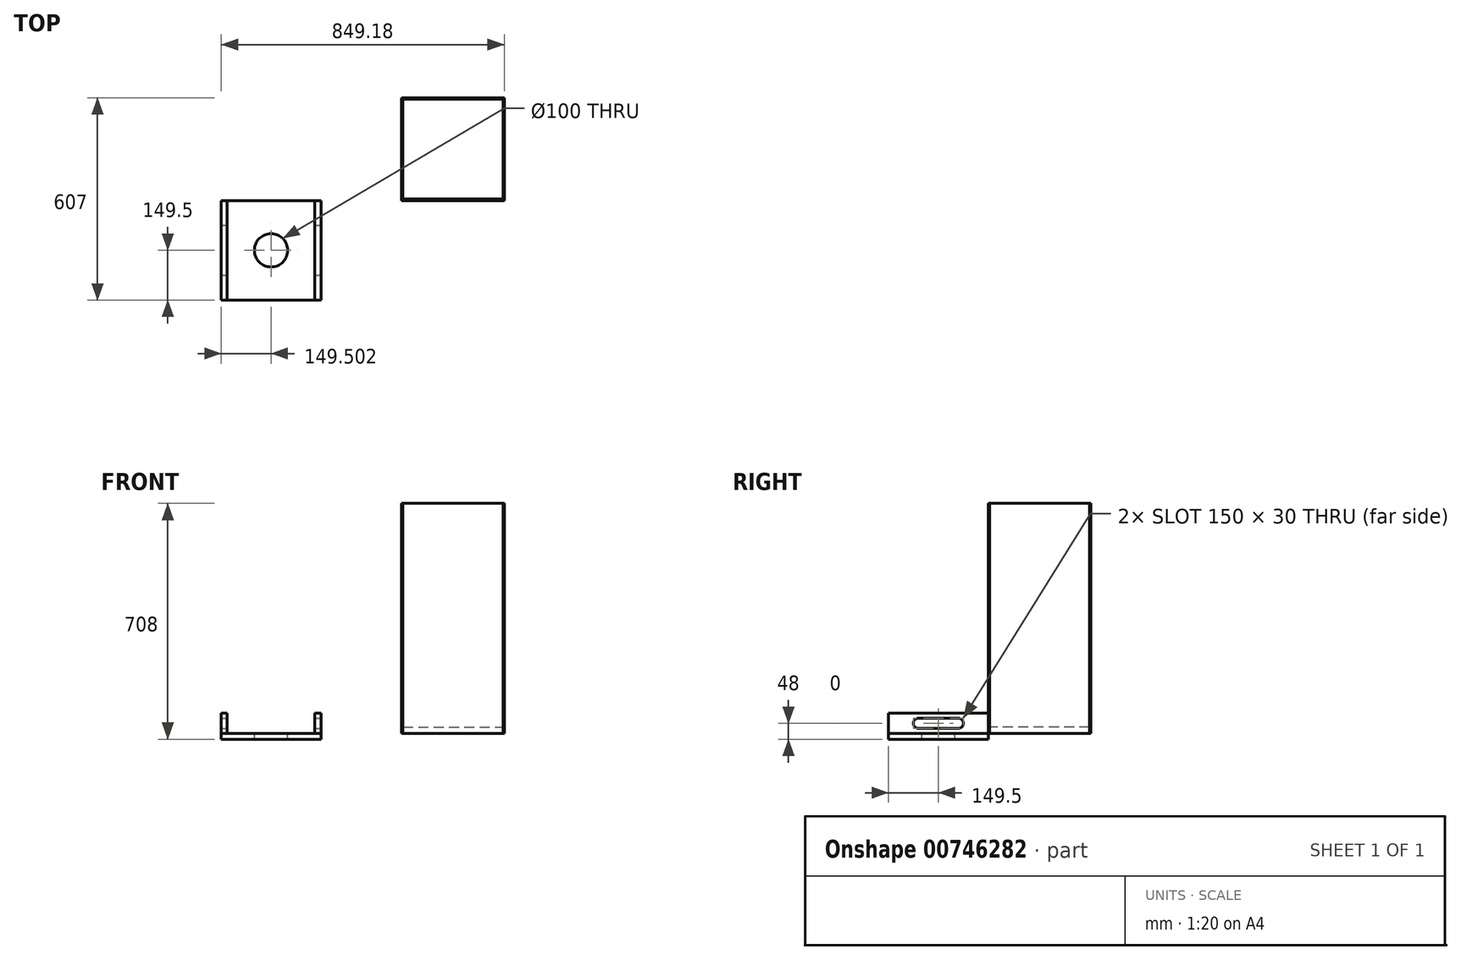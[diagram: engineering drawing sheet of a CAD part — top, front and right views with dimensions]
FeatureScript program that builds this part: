
annotation { "Feature Type Name" : "Feature", "Feature Type Description" : "" }
export const myFeature = defineFeature(function(context is Context, id is Id, definition is map)
    precondition{}
    {
        {
            assignVariable(context, id + "F0", {"name" : "Hoehe", "anyValue" : 690});
        }
        {
            var Q0;
            Q0=qCreatedBy(makeId("Top.planeOp"),FACE);
            var sketch = newSketch(context, id + "F1", { "sketchPlane" : qUnion([Q0])});
            skLineSegment(sketch, "E0.bottom", {"start": v(0, 0) * mm, "end": v(308, 0) * mm});
            skLineSegment(sketch, "E0.top", {"start": v(0, 308) * mm, "end": v(308, 308) * mm});
            skLineSegment(sketch, "E0.left", {"start": v(0, 0) * mm, "end": v(0, 308) * mm});
            skLineSegment(sketch, "E0.right", {"start": v(308, 0) * mm, "end": v(308, 308) * mm});
            skLineSegment(sketch, "E1", {"start": v(4, 308) * mm, "end": v(4, 0) * mm});
            skLineSegment(sketch, "E2", {"start": v(0, 4) * mm, "end": v(308, 4) * mm});
            skLineSegment(sketch, "E3", {"start": v(0, 304) * mm, "end": v(308, 304) * mm});
            skLineSegment(sketch, "E4", {"start": v(304, 308) * mm, "end": v(304, 0) * mm});
            skSolve(sketch);
        }
        {
            var Q0;
            {var subQ0=sQuery(id+"F1.wireOp",EDGE,"E2");var subQ1=sQuery(id+"F1.wireOp",EDGE,"E0.left");var subQ2=makeQuery(id+"F1.imprint","INTERSECT",VERTEX,{"derivedFrom":[subQ1,subQ0]});Q0=makeQuery(id+"F1.imprint","IMPRINT",FACE,{"disambiguationData":[TD([[makeQuery(id+"F1.imprint","IMPRINT",EDGE,{"disambiguationData":[TD([[subQ2,-1.0]])],"derivedFrom":subQ1}),-1.0]])]});}
            var Q1;
            {var subQ0=sQuery(id+"F1.wireOp",EDGE,"E2");var subQ1=sQuery(id+"F1.wireOp",EDGE,"E0.right");var subQ2=makeQuery(id+"F1.imprint","INTERSECT",VERTEX,{"derivedFrom":[subQ1,subQ0]});Q1=makeQuery(id+"F1.imprint","IMPRINT",FACE,{"disambiguationData":[TD([[makeQuery(id+"F1.imprint","IMPRINT",EDGE,{"disambiguationData":[TD([[subQ2,-1.0]])],"derivedFrom":subQ1}),1.0]])]});}
            var Q2;
            {var subQ0=sQuery(id+"F1.wireOp",EDGE,"E0.right");var subQ1=sQuery(id+"F1.wireOp",EDGE,"E0.top");var subQ2=makeQuery(id+"F1.imprint","INTERSECT",VERTEX,{"derivedFrom":[subQ1,subQ0]});Q2=makeQuery(id+"F1.imprint","IMPRINT",FACE,{"disambiguationData":[TD([[makeQuery(id+"F1.imprint","IMPRINT",EDGE,{"disambiguationData":[TD([[subQ2,1.0]])],"derivedFrom":subQ1}),-1.0]])]});}
            var Q3;
            {var subQ0=sQuery(id+"F1.wireOp",EDGE,"E0.left");var subQ1=sQuery(id+"F1.wireOp",EDGE,"E0.top");var subQ2=makeQuery(id+"F1.imprint","INTERSECT",VERTEX,{"derivedFrom":[subQ1,subQ0]});Q3=makeQuery(id+"F1.imprint","IMPRINT",FACE,{"disambiguationData":[TD([[makeQuery(id+"F1.imprint","IMPRINT",EDGE,{"disambiguationData":[TD([[subQ2,-1.0]])],"derivedFrom":subQ1}),-1.0]])]});}
            var Q4;
            {var subQ0=sQuery(id+"F1.wireOp",EDGE,"E0.right");var subQ1=sQuery(id+"F1.wireOp",EDGE,"E0.bottom");var subQ2=makeQuery(id+"F1.imprint","INTERSECT",VERTEX,{"derivedFrom":[subQ1,subQ0]});Q4=makeQuery(id+"F1.imprint","IMPRINT",FACE,{"disambiguationData":[TD([[makeQuery(id+"F1.imprint","IMPRINT",EDGE,{"disambiguationData":[TD([[subQ2,1.0]])],"derivedFrom":subQ1}),1.0]])]});}
            var Q5;
            {var subQ0=sQuery(id+"F1.wireOp",EDGE,"E0.left");var subQ1=sQuery(id+"F1.wireOp",EDGE,"E0.bottom");var subQ2=makeQuery(id+"F1.imprint","INTERSECT",VERTEX,{"derivedFrom":[subQ1,subQ0]});Q5=makeQuery(id+"F1.imprint","IMPRINT",FACE,{"disambiguationData":[TD([[makeQuery(id+"F1.imprint","IMPRINT",EDGE,{"disambiguationData":[TD([[subQ2,-1.0]])],"derivedFrom":subQ1}),1.0]])]});}
            extrude(context, id + "F2", {"entities" : qUnion([Q0, Q1, Q2, Q3, Q4, Q5]), "depth" : (getVariable(context, 'Hoehe')) * mm, "offsetDistance" : 25 * mm});
        }
        {
            var Q0;
            {var subQ0=sQuery(id+"F1.wireOp",EDGE,"E1");var subQ1=sQuery(id+"F1.wireOp",EDGE,"E0.bottom");var subQ2=makeQuery(id+"F1.imprint","INTERSECT",VERTEX,{"derivedFrom":[subQ1,subQ0]});Q0=makeQuery(id+"F1.imprint","IMPRINT",FACE,{"disambiguationData":[TD([[makeQuery(id+"F1.imprint","IMPRINT",EDGE,{"disambiguationData":[TD([[subQ2,-1.0]])],"derivedFrom":subQ1}),1.0]])]});}
            var Q1;
            {var subQ0=sQuery(id+"F1.wireOp",EDGE,"E0.left");var subQ1=sQuery(id+"F1.wireOp",EDGE,"E0.bottom");var subQ2=makeQuery(id+"F1.imprint","INTERSECT",VERTEX,{"derivedFrom":[subQ1,subQ0]});Q1=makeQuery(id+"F1.imprint","IMPRINT",FACE,{"disambiguationData":[TD([[makeQuery(id+"F1.imprint","IMPRINT",EDGE,{"disambiguationData":[TD([[subQ2,-1.0]])],"derivedFrom":subQ1}),1.0]])]});}
            var Q2;
            {var subQ0=sQuery(id+"F1.wireOp",EDGE,"E0.right");var subQ1=sQuery(id+"F1.wireOp",EDGE,"E0.bottom");var subQ2=makeQuery(id+"F1.imprint","INTERSECT",VERTEX,{"derivedFrom":[subQ1,subQ0]});Q2=makeQuery(id+"F1.imprint","IMPRINT",FACE,{"disambiguationData":[TD([[makeQuery(id+"F1.imprint","IMPRINT",EDGE,{"disambiguationData":[TD([[subQ2,1.0]])],"derivedFrom":subQ1}),1.0]])]});}
            var Q3;
            {var subQ0=sQuery(id+"F1.wireOp",EDGE,"E0.right");var subQ1=sQuery(id+"F1.wireOp",EDGE,"E0.top");var subQ2=makeQuery(id+"F1.imprint","INTERSECT",VERTEX,{"derivedFrom":[subQ1,subQ0]});Q3=makeQuery(id+"F1.imprint","IMPRINT",FACE,{"disambiguationData":[TD([[makeQuery(id+"F1.imprint","IMPRINT",EDGE,{"disambiguationData":[TD([[subQ2,1.0]])],"derivedFrom":subQ1}),-1.0]])]});}
            var Q4;
            {var subQ0=sQuery(id+"F1.wireOp",EDGE,"E1");var subQ1=sQuery(id+"F1.wireOp",EDGE,"E0.top");var subQ2=makeQuery(id+"F1.imprint","INTERSECT",VERTEX,{"derivedFrom":[subQ1,subQ0]});Q4=makeQuery(id+"F1.imprint","IMPRINT",FACE,{"disambiguationData":[TD([[makeQuery(id+"F1.imprint","IMPRINT",EDGE,{"disambiguationData":[TD([[subQ2,-1.0]])],"derivedFrom":subQ1}),-1.0]])]});}
            var Q5;
            {var subQ0=sQuery(id+"F1.wireOp",EDGE,"E0.left");var subQ1=sQuery(id+"F1.wireOp",EDGE,"E0.top");var subQ2=makeQuery(id+"F1.imprint","INTERSECT",VERTEX,{"derivedFrom":[subQ1,subQ0]});Q5=makeQuery(id+"F1.imprint","IMPRINT",FACE,{"disambiguationData":[TD([[makeQuery(id+"F1.imprint","IMPRINT",EDGE,{"disambiguationData":[TD([[subQ2,-1.0]])],"derivedFrom":subQ1}),-1.0]])]});}
            extrude(context, id + "F3", {"entities" : qUnion([Q0, Q1, Q2, Q3, Q4, Q5]), "depth" : (getVariable(context, 'Hoehe')) * mm, "offsetDistance" : 25 * mm});
        }
        {
            var Q0;
            {var subQ0=sQuery(id+"F1.wireOp",EDGE,"E3");var subQ1=sQuery(id+"F1.wireOp",EDGE,"E1");var subQ2=makeQuery(id+"F1.imprint","INTERSECT",VERTEX,{"derivedFrom":[subQ1,subQ0]});Q0=makeQuery(id+"F1.imprint","IMPRINT",FACE,{"disambiguationData":[TD([[makeQuery(id+"F1.imprint","IMPRINT",EDGE,{"disambiguationData":[TD([[subQ2,-1.0]])],"derivedFrom":subQ1}),1.0]])]});}
            extrude(context, id + "F4", {"entities" : qUnion([Q0]), "depth" : 19 * mm, "offsetDistance" : 25 * mm});
        }
        {
            var Q0;
            Q0=qCreatedBy(makeId("Top.planeOp"),FACE);
            var sketch = newSketch(context, id + "F5", { "sketchPlane" : qUnion([Q0])});
            skLineSegment(sketch, "E5.bottom", {"start": v(-541.18, -299) * mm, "end": v(-242.18, -299) * mm});
            skLineSegment(sketch, "E5.top", {"start": v(-541.18, 0) * mm, "end": v(-242.18, 0) * mm});
            skLineSegment(sketch, "E5.left", {"start": v(-541.18, -299) * mm, "end": v(-541.18, 0) * mm});
            skLineSegment(sketch, "E5.right", {"start": v(-242.18, -299) * mm, "end": v(-242.18, 0) * mm});
            skLineSegment(sketch, "E6", {"start": v(-391.68, 0) * mm, "end": v(-391.68, -299) * mm, "construction": true});
            skLineSegment(sketch, "E7", {"start": v(-541.18, -149.5) * mm, "end": v(-242.18, -149.5) * mm, "construction": true});
            skCircle(sketch, "E8", {"center": v(-391.68, -149.5) * mm, "radius": 50 * mm});
            skLineSegment(sketch, "E9", {"start": v(-523.18, 0) * mm, "end": v(-523.18, -299) * mm});
            skLineSegment(sketch, "E10", {"start": v(-260.18, 0) * mm, "end": v(-260.18, -299) * mm});
            skLineSegment(sketch, "E11.bottom", {"start": v(173.44, -497.88) * mm, "end": v(472.44, -497.88) * mm});
            skLineSegment(sketch, "E11.top", {"start": v(173.44, -198.88) * mm, "end": v(472.44, -198.88) * mm});
            skLineSegment(sketch, "E11.left", {"start": v(173.44, -497.88) * mm, "end": v(173.44, -198.88) * mm});
            skLineSegment(sketch, "E11.right", {"start": v(472.44, -497.88) * mm, "end": v(472.44, -198.88) * mm});
            skLineSegment(sketch, "E12", {"start": v(322.94, -198.88) * mm, "end": v(322.94, -497.88) * mm, "construction": true});
            skLineSegment(sketch, "E13", {"start": v(173.44, -348.38) * mm, "end": v(472.44, -348.38) * mm, "construction": true});
            skLineSegment(sketch, "E14", {"start": v(177.44, -198.88) * mm, "end": v(177.44, -497.88) * mm});
            skLineSegment(sketch, "E15", {"start": v(468.44, -198.88) * mm, "end": v(468.44, -497.88) * mm});
            skLineSegment(sketch, "E16", {"start": v(203.36, -198.88) * mm, "end": v(203.36, -497.88) * mm});
            skSolve(sketch);
        }
        {
            var Q0;
            Q0=makeQuery(id+"F5.imprint","IMPRINT",FACE,{"disambiguationData":[TD([[makeQuery(id+"F5.imprint","IMPRINT",EDGE,{"derivedFrom":sQuery(id+"F5.wireOp",EDGE,"E5.bottom")}),1.0]])]});
            var Q1;
            Q1=makeQuery(id+"F5.imprint","IMPRINT",FACE,{"disambiguationData":[TD([[makeQuery(id+"F5.imprint","IMPRINT",EDGE,{"derivedFrom":sQuery(id+"F5.wireOp",EDGE,"E8")}),-1.0]])]});
            extrude(context, id + "F6", {"entities" : qUnion([Q0, Q1]), "oppositeDirection" : true, "depth" : 18 * mm, "offsetDistance" : 25 * mm});
        }
        {
            var Q0;
            {var subQ0=sQuery(id+"F5.wireOp",EDGE,"E5.left");Q0=makeQuery(id+"F5.imprint","IMPRINT",FACE,{"disambiguationData":[TD([[makeQuery(id+"F5.imprint","IMPRINT",EDGE,{"derivedFrom":subQ0}),-1.0]])]});}
            var Q1;
            {var subQ0=sQuery(id+"F5.wireOp",EDGE,"E5.right");Q1=makeQuery(id+"F5.imprint","IMPRINT",FACE,{"disambiguationData":[TD([[makeQuery(id+"F5.imprint","IMPRINT",EDGE,{"derivedFrom":subQ0}),1.0]])]});}
            extrude(context, id + "F7", {"entities" : qUnion([Q0, Q1]), "depth" : 60 * mm, "offsetDistance" : 25 * mm});
        }
        {
            var Q0;
            Q0=makeQuery(id+"F7.opExtrude","SWEPT_FACE",FACE,{"disambiguationData":[OSD([sQuery(id+"F5.wireOp",EDGE,"E5.right")])]});
            var sketch = newSketch(context, id + "F8", { "sketchPlane" : qUnion([Q0])});
            skPoint(sketch, "E17", {"position": v(-149.5, 60) * mm});
            skLineSegment(sketch, "E18", {"start": v(-149.5, 60) * mm, "end": v(-149.5, 0) * mm, "construction": true});
            skLineSegment(sketch, "E19.bottom", {"start": v(-209.5, 45) * mm, "end": v(-89.5, 45) * mm});
            skLineSegment(sketch, "E19.top", {"start": v(-209.5, 15) * mm, "end": v(-89.5, 15) * mm});
            skArc(sketch, "E20", {"start": v(-209.5, 45) * mm, "mid": v(-224.5, 30) * mm, "end": v(-209.5, 15) * mm});
            skArc(sketch, "E21", {"start": v(-89.5, 15) * mm, "mid": v(-74.5, 30) * mm, "end": v(-89.5, 45) * mm});
            skSolve(sketch);
        }
        {
            var Q0;
            Q0 = qSketchRegion(id + "F8", true);
            extrude(context, id + "F9", {"entities" : qUnion([Q0]), "operationType" : NewBodyOperationType.REMOVE, "endBound" : BoundingType.THROUGH_ALL, "oppositeDirection" : true, "depth" : 25 * mm, "offsetDistance" : 25 * mm});
        }
    });
